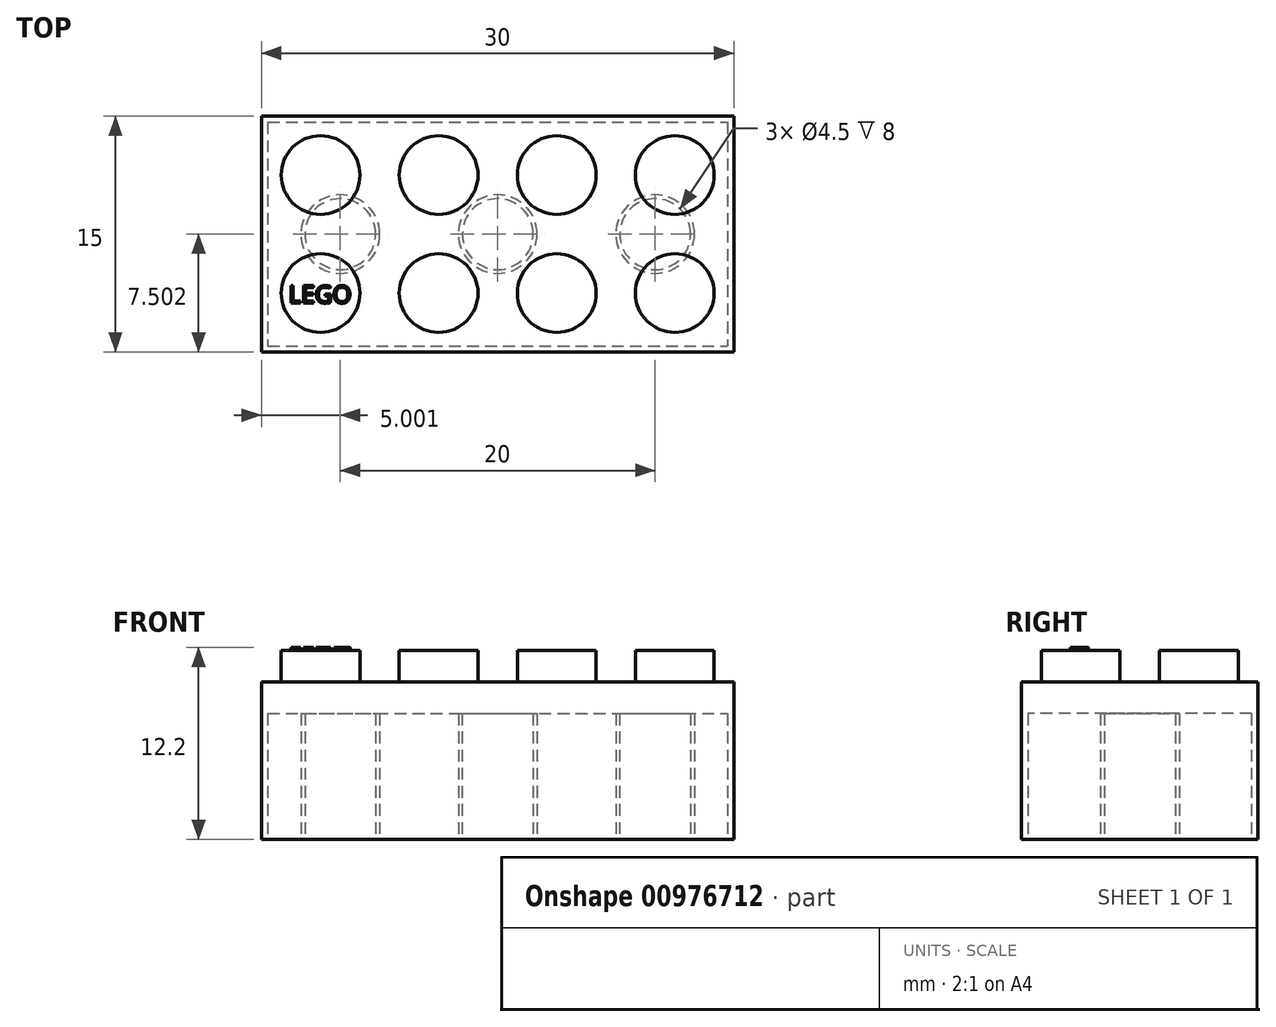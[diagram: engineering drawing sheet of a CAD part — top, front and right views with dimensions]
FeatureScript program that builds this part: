
annotation { "Feature Type Name" : "Feature", "Feature Type Description" : "" }
export const myFeature = defineFeature(function(context is Context, id is Id, definition is map)
    precondition{}
    {
        {
            var Q0;
            Q0=qCreatedBy(makeId("Top.planeOp"),FACE);
            var sketch = newSketch(context, id + "F0", { "sketchPlane" : qUnion([Q0])});
            skLineSegment(sketch, "E0.bottom", {"start": v(-12.65, 7.98) * mm, "end": v(17.35, 7.98) * mm});
            skLineSegment(sketch, "E0.top", {"start": v(-12.65, -7.02) * mm, "end": v(17.35, -7.02) * mm});
            skLineSegment(sketch, "E0.left", {"start": v(-12.65, 7.98) * mm, "end": v(-12.65, -7.02) * mm});
            skLineSegment(sketch, "E0.right", {"start": v(17.35, 7.98) * mm, "end": v(17.35, -7.02) * mm});
            skSolve(sketch);
        }
        {
            var Q0;
            Q0=makeQuery(id+"F0.imprint","IMPRINT",FACE,{"disambiguationData":[TD([[makeQuery(id+"F0.imprint","IMPRINT",EDGE,{"derivedFrom":sQuery(id+"F0.wireOp",EDGE,"E0.bottom")}),-1.0]])]});
            extrude(context, id + "F1", {"entities" : qUnion([Q0]), "depth" : 10 * mm, "offsetDistance" : 25 * mm});
        }
        {
            var Q0;
            Q0=makeQuery(id+"F1.opExtrude","CAP_FACE",FACE,{"disambiguationData":[OSD([sQuery(id+"F0.wireOp",EDGE,"E0.bottom"),sQuery(id+"F0.wireOp",EDGE,"E0.top"),sQuery(id+"F0.wireOp",EDGE,"E0.left"),sQuery(id+"F0.wireOp",EDGE,"E0.right")])],"isStart":false});
            var sketch = newSketch(context, id + "F2", { "sketchPlane" : qUnion([Q0])});
            skCircle(sketch, "E1", {"center": v(-8.9, 4.23) * mm, "radius": 2.5 * mm});
            skCircle(sketch, "E2.1.0.0", {"center": v(-1.4, 4.23) * mm, "radius": 2.5 * mm});
            skCircle(sketch, "E2.2.0.0", {"center": v(6.1, 4.23) * mm, "radius": 2.5 * mm});
            skCircle(sketch, "E2.3.0.0", {"center": v(13.6, 4.23) * mm, "radius": 2.5 * mm});
            skLineSegment(sketch, "E2.direction1", {"start": v(-8.9, 4.23) * mm, "end": v(-1.4, 4.23) * mm, "construction": true});
            skCircle(sketch, "E3.1.0.0", {"center": v(-8.9, -3.27) * mm, "radius": 2.5 * mm});
            skCircle(sketch, "E3.1.0.1", {"center": v(-1.4, -3.27) * mm, "radius": 2.5 * mm});
            skCircle(sketch, "E3.1.0.2", {"center": v(6.1, -3.27) * mm, "radius": 2.5 * mm});
            skCircle(sketch, "E3.1.0.3", {"center": v(13.6, -3.27) * mm, "radius": 2.5 * mm});
            skLineSegment(sketch, "E3.direction1", {"start": v(-8.9, 4.23) * mm, "end": v(-8.9, -3.27) * mm, "construction": true});
            skSolve(sketch);
        }
        {
            var Q0;
            Q0=makeQuery(id+"F2.imprint","IMPRINT",FACE,{"disambiguationData":[TD([[makeQuery(id+"F2.imprint","IMPRINT",EDGE,{"derivedFrom":sQuery(id+"F2.wireOp",EDGE,"E1")}),1.0]])]});
            var Q1;
            Q1=makeQuery(id+"F2.imprint","IMPRINT",FACE,{"disambiguationData":[TD([[makeQuery(id+"F2.imprint","IMPRINT",EDGE,{"derivedFrom":sQuery(id+"F2.wireOp",EDGE,"E2.1.0.0")}),1.0]])]});
            var Q2;
            Q2=makeQuery(id+"F2.imprint","IMPRINT",FACE,{"disambiguationData":[TD([[makeQuery(id+"F2.imprint","IMPRINT",EDGE,{"derivedFrom":sQuery(id+"F2.wireOp",EDGE,"E2.2.0.0")}),1.0]])]});
            var Q3;
            Q3=makeQuery(id+"F2.imprint","IMPRINT",FACE,{"disambiguationData":[TD([[makeQuery(id+"F2.imprint","IMPRINT",EDGE,{"derivedFrom":sQuery(id+"F2.wireOp",EDGE,"E2.3.0.0")}),1.0]])]});
            var Q4;
            Q4=makeQuery(id+"F2.imprint","IMPRINT",FACE,{"disambiguationData":[TD([[makeQuery(id+"F2.imprint","IMPRINT",EDGE,{"derivedFrom":sQuery(id+"F2.wireOp",EDGE,"E3.1.0.3")}),1.0]])]});
            var Q5;
            Q5=makeQuery(id+"F2.imprint","IMPRINT",FACE,{"disambiguationData":[TD([[makeQuery(id+"F2.imprint","IMPRINT",EDGE,{"derivedFrom":sQuery(id+"F2.wireOp",EDGE,"E3.1.0.2")}),1.0]])]});
            var Q6;
            Q6=makeQuery(id+"F2.imprint","IMPRINT",FACE,{"disambiguationData":[TD([[makeQuery(id+"F2.imprint","IMPRINT",EDGE,{"derivedFrom":sQuery(id+"F2.wireOp",EDGE,"E3.1.0.1")}),1.0]])]});
            var Q7;
            Q7=makeQuery(id+"F2.imprint","IMPRINT",FACE,{"disambiguationData":[TD([[makeQuery(id+"F2.imprint","IMPRINT",EDGE,{"derivedFrom":sQuery(id+"F2.wireOp",EDGE,"E3.1.0.0")}),1.0]])]});
            extrude(context, id + "F3", {"entities" : qUnion([Q0, Q1, Q2, Q3, Q4, Q5, Q6, Q7]), "operationType" : NewBodyOperationType.ADD, "depth" : 2 * mm, "offsetDistance" : 25 * mm});
        }
        {
            var Q0;
            Q0=makeQuery(id+"F1.opExtrude","CAP_FACE",FACE,{"disambiguationData":[OSD([sQuery(id+"F0.wireOp",EDGE,"E0.bottom"),sQuery(id+"F0.wireOp",EDGE,"E0.top"),sQuery(id+"F0.wireOp",EDGE,"E0.left"),sQuery(id+"F0.wireOp",EDGE,"E0.right")])],"isStart":true});
            var sketch = newSketch(context, id + "F4", { "sketchPlane" : qUnion([Q0])});
            skLineSegment(sketch, "E4", {"start": v(2.35, 7.02) * mm, "end": v(2.35, -7.98) * mm, "construction": true});
            skCircle(sketch, "E5", {"center": v(2.35, -0.48) * mm, "radius": 2.5 * mm});
            skCircle(sketch, "E6", {"center": v(-7.65, -0.48) * mm, "radius": 2.5 * mm});
            skCircle(sketch, "E7", {"center": v(12.35, -0.48) * mm, "radius": 2.5 * mm});
            skLineSegment(sketch, "E8", {"start": v(17.35, -0.48) * mm, "end": v(12.35, -0.48) * mm, "construction": true});
            skLineSegment(sketch, "E9", {"start": v(12.35, -0.48) * mm, "end": v(2.35, -0.48) * mm, "construction": true});
            skLineSegment(sketch, "E10", {"start": v(2.35, -0.48) * mm, "end": v(-7.65, -0.48) * mm, "construction": true});
            skLineSegment(sketch, "E11", {"start": v(-7.65, -0.48) * mm, "end": v(-12.65, -0.48) * mm, "construction": true});
            skCircle(sketch, "E12", {"center": v(-7.65, -0.48) * mm, "radius": 2.25 * mm});
            skCircle(sketch, "E13", {"center": v(2.35, -0.48) * mm, "radius": 2.25 * mm});
            skCircle(sketch, "E14", {"center": v(12.35, -0.48) * mm, "radius": 2.25 * mm});
            skLineSegment(sketch, "E15.0", {"start": v(16.95, -7.58) * mm, "end": v(16.95, 6.62) * mm});
            skLineSegment(sketch, "E15.1", {"start": v(-12.25, -7.58) * mm, "end": v(16.95, -7.58) * mm});
            skLineSegment(sketch, "E15.2", {"start": v(-12.25, -7.58) * mm, "end": v(-12.25, 6.62) * mm});
            skLineSegment(sketch, "E15.3", {"start": v(-12.25, 6.62) * mm, "end": v(16.95, 6.62) * mm});
            skSolve(sketch);
        }
        {
            var Q0;
            Q0=makeQuery(id+"F4.imprint","IMPRINT",FACE,{"disambiguationData":[TD([[makeQuery(id+"F4.imprint","IMPRINT",EDGE,{"derivedFrom":sQuery(id+"F4.wireOp",EDGE,"E5")}),-1.0]])]});
            var Q1;
            Q1=makeQuery(id+"F4.imprint","IMPRINT",FACE,{"disambiguationData":[TD([[makeQuery(id+"F4.imprint","IMPRINT",EDGE,{"derivedFrom":sQuery(id+"F4.wireOp",EDGE,"E12")}),1.0]])]});
            var Q2;
            Q2=makeQuery(id+"F4.imprint","IMPRINT",FACE,{"disambiguationData":[TD([[makeQuery(id+"F4.imprint","IMPRINT",EDGE,{"derivedFrom":sQuery(id+"F4.wireOp",EDGE,"E13")}),1.0]])]});
            var Q3;
            Q3=makeQuery(id+"F4.imprint","IMPRINT",FACE,{"disambiguationData":[TD([[makeQuery(id+"F4.imprint","IMPRINT",EDGE,{"derivedFrom":sQuery(id+"F4.wireOp",EDGE,"E14")}),1.0]])]});
            extrude(context, id + "F5", {"entities" : qUnion([Q0, Q1, Q2, Q3]), "operationType" : NewBodyOperationType.REMOVE, "oppositeDirection" : true, "depth" : 8 * mm, "offsetDistance" : 25 * mm});
        }
        {
            var Q0;
            Q0=makeQuery(id+"F3.opExtrude","CAP_FACE",FACE,{"disambiguationData":[OSD([sQuery(id+"F2.wireOp",EDGE,"E3.1.0.0")])],"isStart":false});
            var sketch = newSketch(context, id + "F6", { "sketchPlane" : qUnion([Q0])});
            skText(sketch, "E16", { "text": "LEGO", "fontName": "OpenSans-Regular.ttf"});
            const initialGuessF6  = {"E16": [-0.01092, -0.0039, 1, 0, 0.00111]};
            skSetInitialGuess(sketch, initialGuessF6);
            skSolve(sketch);
        }
        {
            var Q0;
            Q0 = qSketchRegion(id + "F6", true);
            extrude(context, id + "F7", {"entities" : qUnion([Q0]), "operationType" : NewBodyOperationType.ADD, "depth" : 0.2 * mm, "offsetDistance" : 25 * mm});
        }
    });
